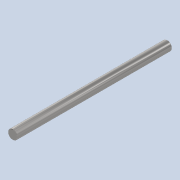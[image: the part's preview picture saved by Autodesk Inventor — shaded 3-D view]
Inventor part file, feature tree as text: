
AUTODESK INVENTOR PART (.ipt)
format: ipt  version: 2020 (Build 240168000, 168)  size: 86,016 bytes
history: native  units: mm
features: extrude x1, chamfer x1, sketch x1
ambient origin geometry x8: Origin, YZ Plane, XZ Plane, XY Plane, X Axis, Y Axis, Z Axis, Center Point
bodies: Solid1 (feature_tree)
feature tree (3):
  extrude  "Extrusion1"  Depth=166.0mm TaperAngle=0.0deg
  chamfer  "Chamfer1"  Distance=0.5mm Angle=45.0deg
  sketch  "Sketch1"  dims[d0=10.0mm d1=166.0mm d2=0.0mm d3=0.5mm d4=2.0mm d5=45.0deg]
